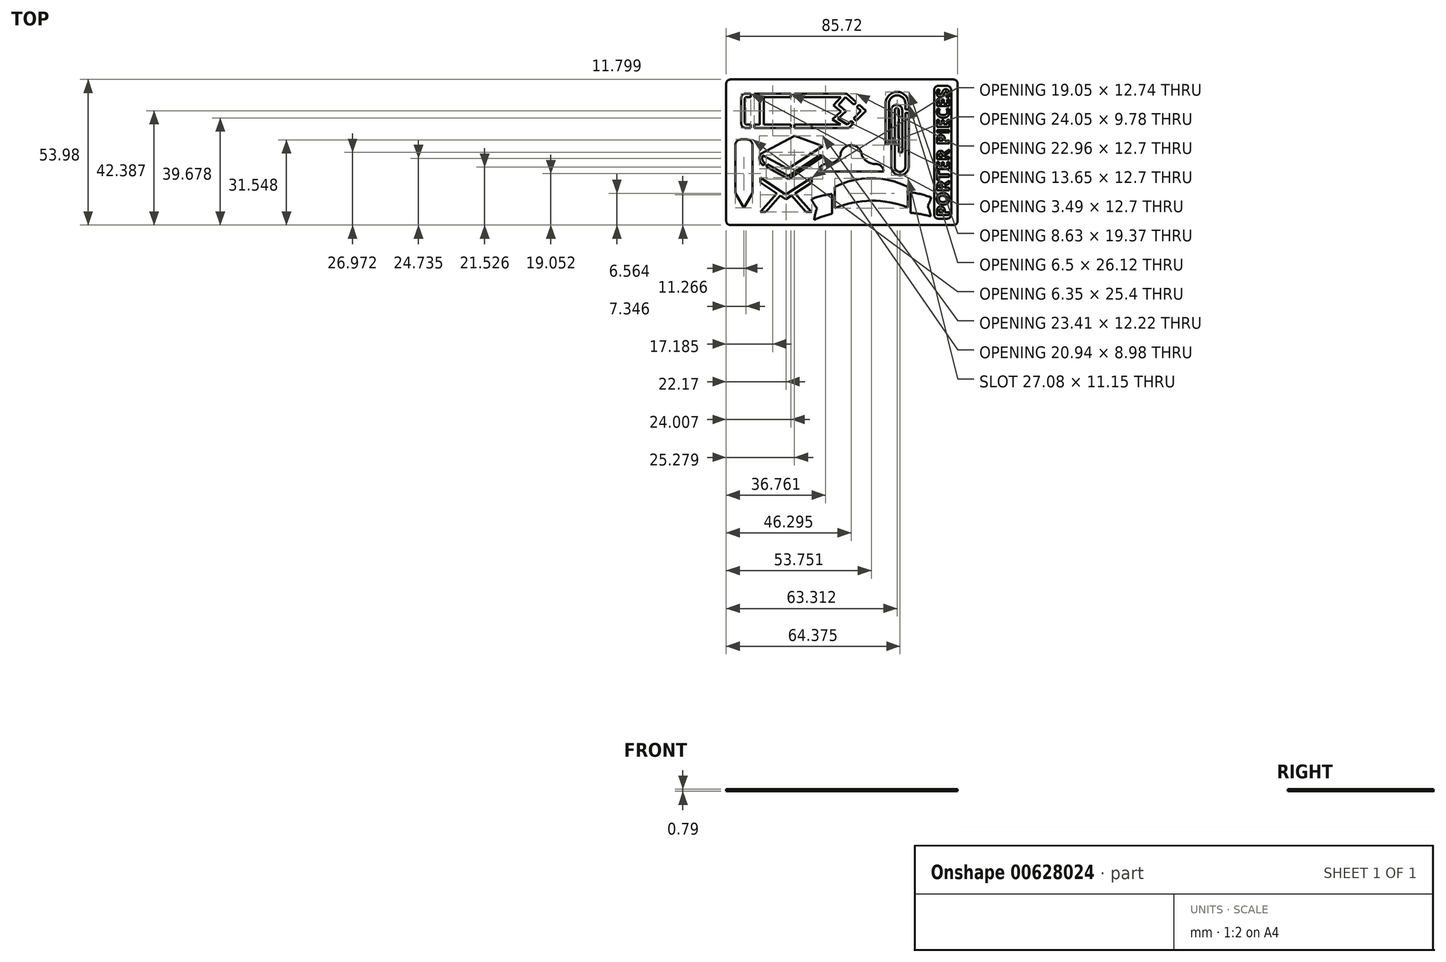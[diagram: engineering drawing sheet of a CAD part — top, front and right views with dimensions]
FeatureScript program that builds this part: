
annotation { "Feature Type Name" : "Feature", "Feature Type Description" : "" }
export const myFeature = defineFeature(function(context is Context, id is Id, definition is map)
    precondition{}
    {
        {
            var Q0;
            Q0=qCreatedBy(makeId("Top.planeOp"),FACE);
            var sketch = newSketch(context, id + "F0", { "sketchPlane" : qUnion([Q0])});
            skLineSegment(sketch, "E0.bottom", {"start": v(42.86, 26.99) * mm, "end": v(-42.86, 26.99) * mm});
            skLineSegment(sketch, "E0.top", {"start": v(42.86, -26.99) * mm, "end": v(-42.86, -26.99) * mm});
            skLineSegment(sketch, "E0.left", {"start": v(42.86, 26.99) * mm, "end": v(42.86, -26.99) * mm});
            skLineSegment(sketch, "E0.right", {"start": v(-42.86, 26.99) * mm, "end": v(-42.86, -26.99) * mm});
            skPoint(sketch, "E0.middle", {"position": v(0, 0) * mm});
            skSolve(sketch);
        }
        {
            var Q0;
            Q0=makeQuery(id+"F0.imprint","IMPRINT",FACE,{"disambiguationData":[TD([[makeQuery(id+"F0.imprint","IMPRINT",EDGE,{"derivedFrom":sQuery(id+"F0.wireOp",EDGE,"E0.bottom")}),1.0]])]});
            extrude(context, id + "F1", {"entities" : qUnion([Q0]), "depth" : 0.8 * mm, "offsetDistance" : 25.4 * mm});
        }
        {
            var Q0;
            Q0=makeQuery(id+"F1.opExtrude","SWEPT_EDGE",EDGE,{"disambiguationData":[OSD([sQuery(id+"F0.wireOp",EDGE,"E0.bottom"),sQuery(id+"F0.wireOp",EDGE,"E0.left")])]});
            var Q1;
            Q1=makeQuery(id+"F1.opExtrude","SWEPT_EDGE",EDGE,{"disambiguationData":[OSD([sQuery(id+"F0.wireOp",EDGE,"E0.bottom"),sQuery(id+"F0.wireOp",EDGE,"E0.right")])]});
            var Q2;
            Q2=makeQuery(id+"F1.opExtrude","SWEPT_EDGE",EDGE,{"disambiguationData":[OSD([sQuery(id+"F0.wireOp",EDGE,"E0.top"),sQuery(id+"F0.wireOp",EDGE,"E0.right")])]});
            var Q3;
            Q3=makeQuery(id+"F1.opExtrude","SWEPT_EDGE",EDGE,{"disambiguationData":[OSD([sQuery(id+"F0.wireOp",EDGE,"E0.top"),sQuery(id+"F0.wireOp",EDGE,"E0.left")])]});
            fillet(context, id + "F2", {"entities" : qUnion([Q0, Q1, Q2, Q3]), "radius" : 1.59 * mm, "tangentPropagation" : true, "allowEdgeOverflow" : false});
        }
        {
            var Q0;
            Q0=makeQuery(id+"F1.opExtrude","CAP_FACE",FACE,{"disambiguationData":[OSD([sQuery(id+"F0.wireOp",EDGE,"E0.bottom"),sQuery(id+"F0.wireOp",EDGE,"E0.top"),sQuery(id+"F0.wireOp",EDGE,"E0.left"),sQuery(id+"F0.wireOp",EDGE,"E0.right")])],"isStart":false});
            var sketch = newSketch(context, id + "F3", { "sketchPlane" : qUnion([Q0])});
            skLineSegment(sketch, "E1.bottom", {"start": v(34.13, -24.6) * mm, "end": v(40.48, -24.6) * mm});
            skLineSegment(sketch, "E1.top", {"start": v(34.13, 24.6) * mm, "end": v(40.48, 24.6) * mm});
            skLineSegment(sketch, "E1.left", {"start": v(34.13, -24.6) * mm, "end": v(34.13, 24.6) * mm});
            skLineSegment(sketch, "E1.right", {"start": v(40.48, -24.6) * mm, "end": v(40.48, 24.6) * mm});
            skSolve(sketch);
        }
        {
            var Q0;
            Q0=makeQuery(id+"F3.imprint","IMPRINT",FACE,{"disambiguationData":[TD([[makeQuery(id+"F3.imprint","IMPRINT",EDGE,{"derivedFrom":sQuery(id+"F3.wireOp",EDGE,"E1.bottom")}),1.0]])]});
            extrude(context, id + "F4", {"entities" : qUnion([Q0]), "operationType" : NewBodyOperationType.REMOVE, "oppositeDirection" : true, "depth" : 0.4 * mm, "offsetDistance" : 25.4 * mm});
        }
        {
            var Q0;
            Q0=makeQuery(id+"F4.boolean.opBoolean","COPY",EDGE,{"derivedFrom":makeQuery(id+"F4.opExtrude","SWEPT_EDGE",EDGE,{"disambiguationData":[OSD([sQuery(id+"F3.wireOp",EDGE,"E1.bottom"),sQuery(id+"F3.wireOp",EDGE,"E1.left")])]})});
            var Q1;
            Q1=makeQuery(id+"F4.boolean.opBoolean","COPY",EDGE,{"derivedFrom":makeQuery(id+"F4.opExtrude","SWEPT_EDGE",EDGE,{"disambiguationData":[OSD([sQuery(id+"F3.wireOp",EDGE,"E1.bottom"),sQuery(id+"F3.wireOp",EDGE,"E1.right")])]})});
            var Q2;
            Q2=makeQuery(id+"F4.boolean.opBoolean","COPY",EDGE,{"derivedFrom":makeQuery(id+"F4.opExtrude","SWEPT_EDGE",EDGE,{"disambiguationData":[OSD([sQuery(id+"F3.wireOp",EDGE,"E1.top"),sQuery(id+"F3.wireOp",EDGE,"E1.right")])]})});
            var Q3;
            Q3=makeQuery(id+"F4.boolean.opBoolean","COPY",EDGE,{"derivedFrom":makeQuery(id+"F4.opExtrude","SWEPT_EDGE",EDGE,{"disambiguationData":[OSD([sQuery(id+"F3.wireOp",EDGE,"E1.top"),sQuery(id+"F3.wireOp",EDGE,"E1.left")])]})});
            fillet(context, id + "F5", {"entities" : qUnion([Q0, Q1, Q2, Q3]), "radius" : 1.59 * mm, "tangentPropagation" : true, "allowEdgeOverflow" : false});
        }
        {
            var Q0;
            Q0=makeQuery(id+"F4.boolean.opBoolean","COPY",FACE,{"derivedFrom":makeQuery(id+"F4.opExtrude","CAP_FACE",FACE,{"disambiguationData":[OSD([sQuery(id+"F3.wireOp",EDGE,"E1.bottom"),sQuery(id+"F3.wireOp",EDGE,"E1.top"),sQuery(id+"F3.wireOp",EDGE,"E1.left"),sQuery(id+"F3.wireOp",EDGE,"E1.right")])],"isStart":false})});
            var sketch = newSketch(context, id + "F6", { "sketchPlane" : qUnion([Q0])});
            skText(sketch, "E2", { "text": "PORTER PIECES", "fontName": "OpenSans-Bold.ttf"});
            const initialGuessF6  = {"E2": [0.03976, -0.02381, 0, 1, 0.00461]};
            skSetInitialGuess(sketch, initialGuessF6);
            skSolve(sketch);
        }
        {
            var Q0;
            Q0=makeQuery(id+"F6.imprint","IMPRINT",FACE,{"disambiguationData":[TD([[makeQuery(id+"F6.imprint","IMPRINT",EDGE,{"derivedFrom":sQuery(id+"F6.wireOp",EDGE,"E2.sketch_text.stroke-0")}),-1.0]])]});
            var Q1;
            Q1=makeQuery(id+"F6.imprint","IMPRINT",FACE,{"disambiguationData":[TD([[makeQuery(id+"F6.imprint","IMPRINT",EDGE,{"derivedFrom":sQuery(id+"F6.wireOp",EDGE,"E2.sketch_text.stroke-16")}),-1.0]])]});
            var Q2;
            Q2=makeQuery(id+"F6.imprint","IMPRINT",FACE,{"disambiguationData":[TD([[makeQuery(id+"F6.imprint","IMPRINT",EDGE,{"derivedFrom":sQuery(id+"F6.wireOp",EDGE,"E2.sketch_text.stroke-30")}),-1.0]])]});
            var Q3;
            Q3=makeQuery(id+"F6.imprint","IMPRINT",FACE,{"disambiguationData":[TD([[makeQuery(id+"F6.imprint","IMPRINT",EDGE,{"derivedFrom":sQuery(id+"F6.wireOp",EDGE,"E2.sketch_text.stroke-49")}),-1.0]])]});
            var Q4;
            Q4=makeQuery(id+"F6.imprint","IMPRINT",FACE,{"disambiguationData":[TD([[makeQuery(id+"F6.imprint","IMPRINT",EDGE,{"derivedFrom":sQuery(id+"F6.wireOp",EDGE,"E2.sketch_text.stroke-57")}),-1.0]])]});
            var Q5;
            Q5=makeQuery(id+"F6.imprint","IMPRINT",FACE,{"disambiguationData":[TD([[makeQuery(id+"F6.imprint","IMPRINT",EDGE,{"derivedFrom":sQuery(id+"F6.wireOp",EDGE,"E2.sketch_text.stroke-69")}),-1.0]])]});
            var Q6;
            Q6=makeQuery(id+"F6.imprint","IMPRINT",FACE,{"disambiguationData":[TD([[makeQuery(id+"F6.imprint","IMPRINT",EDGE,{"derivedFrom":sQuery(id+"F6.wireOp",EDGE,"E2.sketch_text.stroke-88")}),-1.0]])]});
            var Q7;
            Q7=makeQuery(id+"F6.imprint","IMPRINT",FACE,{"disambiguationData":[TD([[makeQuery(id+"F6.imprint","IMPRINT",EDGE,{"derivedFrom":sQuery(id+"F6.wireOp",EDGE,"E2.sketch_text.stroke-104")}),-1.0]])]});
            var Q8;
            Q8=makeQuery(id+"F6.imprint","IMPRINT",FACE,{"disambiguationData":[TD([[makeQuery(id+"F6.imprint","IMPRINT",EDGE,{"derivedFrom":sQuery(id+"F6.wireOp",EDGE,"E2.sketch_text.stroke-108")}),-1.0]])]});
            var Q9;
            Q9=makeQuery(id+"F6.imprint","IMPRINT",FACE,{"disambiguationData":[TD([[makeQuery(id+"F6.imprint","IMPRINT",EDGE,{"derivedFrom":sQuery(id+"F6.wireOp",EDGE,"E2.sketch_text.stroke-120")}),-1.0]])]});
            var Q10;
            Q10=makeQuery(id+"F6.imprint","IMPRINT",FACE,{"disambiguationData":[TD([[makeQuery(id+"F6.imprint","IMPRINT",EDGE,{"derivedFrom":sQuery(id+"F6.wireOp",EDGE,"E2.sketch_text.stroke-135")}),-1.0]])]});
            var Q11;
            Q11=makeQuery(id+"F6.imprint","IMPRINT",FACE,{"disambiguationData":[TD([[makeQuery(id+"F6.imprint","IMPRINT",EDGE,{"derivedFrom":sQuery(id+"F6.wireOp",EDGE,"E2.sketch_text.stroke-147")}),-1.0]])]});
            extrude(context, id + "F7", {"entities" : qUnion([Q0, Q1, Q2, Q3, Q4, Q5, Q6, Q7, Q8, Q9, Q10, Q11]), "operationType" : NewBodyOperationType.ADD, "depth" : 0.4 * mm, "offsetDistance" : 25.4 * mm});
        }
        {
            var Q0;
            Q0=makeQuery(id+"F1.opExtrude","CAP_FACE",FACE,{"disambiguationData":[OSD([sQuery(id+"F0.wireOp",EDGE,"E0.bottom"),sQuery(id+"F0.wireOp",EDGE,"E0.top"),sQuery(id+"F0.wireOp",EDGE,"E0.left"),sQuery(id+"F0.wireOp",EDGE,"E0.right")])],"isStart":false});
            var sketch = newSketch(context, id + "F8", { "sketchPlane" : qUnion([Q0])});
            skLineSegment(sketch, "E3", {"start": v(-35.74, 21.75) * mm, "end": v(-33.77, 21.75) * mm});
            skLineSegment(sketch, "E4", {"start": v(1.84, 21.75) * mm, "end": v(5.38, 18.54) * mm});
            skLineSegment(sketch, "E5", {"start": v(8.86, 15.4) * mm, "end": v(5.22, 11.74) * mm});
            skLineSegment(sketch, "E6", {"start": v(2.55, 9.05) * mm, "end": v(-17.58, 9.05) * mm});
            skLineSegment(sketch, "E7", {"start": v(-37.26, 10.57) * mm, "end": v(-37.26, 20.22) * mm});
            skLineSegment(sketch, "E8", {"start": v(-37.26, 15.4) * mm, "end": v(17.01, 15.4) * mm, "construction": true});
            skPoint(sketch, "E9.visualSharp", {"position": v(-37.26, 21.75) * mm});
            skArc(sketch, "E9.filletArc", {"start": v(-35.74, 21.75) * mm, "mid": v(-36.81, 21.3) * mm, "end": v(-37.26, 20.22) * mm});
            skPoint(sketch, "E10.visualSharp", {"position": v(-37.26, 9.05) * mm});
            skArc(sketch, "E10.filletArc", {"start": v(-37.26, 10.57) * mm, "mid": v(-36.81, 9.5) * mm, "end": v(-35.74, 9.05) * mm});
            skLineSegment(sketch, "E11.left", {"start": v(-30.5, 20.48) * mm, "end": v(-30.5, 10.32) * mm});
            skLineSegment(sketch, "E11.right", {"start": v(-28.99, 20.48) * mm, "end": v(-28.99, 10.32) * mm});
            skLineSegment(sketch, "E12.0", {"start": v(1.35, 20.48) * mm, "end": v(4.53, 17.6) * mm});
            skLineSegment(sketch, "E12.1", {"start": v(-35.23, 20.48) * mm, "end": v(-33.77, 20.48) * mm});
            skLineSegment(sketch, "E12.2", {"start": v(7.02, 15.35) * mm, "end": v(4.32, 12.63) * mm});
            skLineSegment(sketch, "E12.3", {"start": v(-0.42, 10.32) * mm, "end": v(-17.58, 10.32) * mm});
            skLineSegment(sketch, "E12.4", {"start": v(-36, 11.08) * mm, "end": v(-36, 19.71) * mm});
            skLineSegment(sketch, "E13", {"start": v(1.35, 20.48) * mm, "end": v(-1.3, 17.55) * mm});
            skLineSegment(sketch, "E14", {"start": v(-1.3, 17.55) * mm, "end": v(1.57, 15.23) * mm});
            skLineSegment(sketch, "E15", {"start": v(1.57, 15.23) * mm, "end": v(-1.44, 12.42) * mm});
            skLineSegment(sketch, "E16", {"start": v(-1.44, 12.42) * mm, "end": v(2.02, 10.32) * mm});
            skLineSegment(sketch, "E17.0", {"start": v(-3.53, 12.2) * mm, "end": v(-0.42, 10.32) * mm});
            skLineSegment(sketch, "E17.1", {"start": v(-0.36, 15.16) * mm, "end": v(-3.53, 12.2) * mm});
            skLineSegment(sketch, "E17.2", {"start": v(-3.14, 17.4) * mm, "end": v(-0.36, 15.16) * mm});
            skLineSegment(sketch, "E17.3", {"start": v(-0.37, 20.48) * mm, "end": v(-3.14, 17.4) * mm});
            skLineSegment(sketch, "E18.trimOffspring", {"start": v(-28.99, 20.48) * mm, "end": v(-18.85, 20.48) * mm});
            skLineSegment(sketch, "E19.trimOffspring", {"start": v(-30.5, 10.32) * mm, "end": v(-32.5, 10.32) * mm});
            skPoint(sketch, "E20.visualSharp", {"position": v(-36, 20.48) * mm});
            skArc(sketch, "E20.filletArc", {"start": v(-35.23, 20.48) * mm, "mid": v(-35.77, 20.25) * mm, "end": v(-36, 19.71) * mm});
            skPoint(sketch, "E21.visualSharp", {"position": v(-36, 10.32) * mm});
            skArc(sketch, "E21.filletArc", {"start": v(-36, 11.08) * mm, "mid": v(-35.77, 10.54) * mm, "end": v(-35.23, 10.32) * mm});
            skLineSegment(sketch, "E22.left", {"start": v(-18.85, 21.75) * mm, "end": v(-18.85, 20.48) * mm});
            skLineSegment(sketch, "E22.right", {"start": v(-17.58, 21.75) * mm, "end": v(-17.58, 20.48) * mm});
            skLineSegment(sketch, "E23.trimOffspring", {"start": v(-18.85, 10.32) * mm, "end": v(-18.85, 9.05) * mm});
            skLineSegment(sketch, "E24.trimOffspring", {"start": v(-17.58, 10.32) * mm, "end": v(-17.58, 9.05) * mm});
            skLineSegment(sketch, "E25.trimOffspring", {"start": v(-17.58, 21.75) * mm, "end": v(1.84, 21.75) * mm});
            skLineSegment(sketch, "E26.trimOffspring", {"start": v(-17.58, 20.48) * mm, "end": v(-0.37, 20.48) * mm});
            skLineSegment(sketch, "E27.trimOffspring", {"start": v(-18.85, 10.32) * mm, "end": v(-28.99, 10.32) * mm});
            skLineSegment(sketch, "E28.trimOffspring", {"start": v(-18.85, 9.05) * mm, "end": v(-32.5, 9.05) * mm});
            skLineSegment(sketch, "E29.left", {"start": v(-33.77, 21.75) * mm, "end": v(-33.77, 20.48) * mm});
            skLineSegment(sketch, "E29.right", {"start": v(-32.5, 21.75) * mm, "end": v(-32.5, 20.48) * mm});
            skLineSegment(sketch, "E30.trimOffspring", {"start": v(-32.5, 21.75) * mm, "end": v(-18.85, 21.75) * mm});
            skLineSegment(sketch, "E31.trimOffspring", {"start": v(-32.5, 20.48) * mm, "end": v(-30.5, 20.48) * mm});
            skLineSegment(sketch, "E32.trimOffspring", {"start": v(-32.5, 10.32) * mm, "end": v(-32.5, 9.05) * mm});
            skLineSegment(sketch, "E33.trimOffspring", {"start": v(-33.77, 10.32) * mm, "end": v(-33.77, 9.05) * mm});
            skLineSegment(sketch, "E34.trimOffspring", {"start": v(-33.77, 10.32) * mm, "end": v(-35.23, 10.32) * mm});
            skLineSegment(sketch, "E35.trimOffspring", {"start": v(-33.77, 9.05) * mm, "end": v(-35.74, 9.05) * mm});
            skLineSegment(sketch, "E36.left", {"start": v(5.38, 18.54) * mm, "end": v(4.53, 17.6) * mm});
            skLineSegment(sketch, "E36.right", {"start": v(6.33, 17.69) * mm, "end": v(5.47, 16.74) * mm});
            skLineSegment(sketch, "E37.trimOffspring", {"start": v(5.47, 16.74) * mm, "end": v(7.02, 15.35) * mm});
            skLineSegment(sketch, "E38.trimOffspring", {"start": v(6.33, 17.69) * mm, "end": v(8.86, 15.4) * mm});
            skLineSegment(sketch, "E39.left", {"start": v(3.42, 11.73) * mm, "end": v(4.32, 10.83) * mm});
            skLineSegment(sketch, "E39.right", {"start": v(4.32, 12.63) * mm, "end": v(5.22, 11.74) * mm});
            skLineSegment(sketch, "E40.trimOffspring", {"start": v(3.42, 11.73) * mm, "end": v(2.02, 10.32) * mm});
            skLineSegment(sketch, "E41.trimOffspring", {"start": v(4.32, 10.83) * mm, "end": v(2.55, 9.05) * mm});
            skSolve(sketch);
        }
        {
            var Q0;
            Q0 = qSketchRegion(id + "F8", true);
            extrude(context, id + "F9", {"entities" : qUnion([Q0]), "operationType" : NewBodyOperationType.REMOVE, "oppositeDirection" : true, "depth" : 25.4 * mm, "offsetDistance" : 25.4 * mm});
        }
        {
            var Q0;
            Q0=makeQuery(id+"F1.opExtrude","CAP_FACE",FACE,{"disambiguationData":[OSD([sQuery(id+"F0.wireOp",EDGE,"E0.bottom"),sQuery(id+"F0.wireOp",EDGE,"E0.top"),sQuery(id+"F0.wireOp",EDGE,"E0.left"),sQuery(id+"F0.wireOp",EDGE,"E0.right")])],"isStart":false});
            var sketch = newSketch(context, id + "F10", { "sketchPlane" : qUnion([Q0])});
            skLineSegment(sketch, "E42", {"start": v(17.4, 3) * mm, "end": v(17.4, 18.06) * mm});
            skArc(sketch, "E43", {"start": v(23.5, 18.06) * mm, "mid": v(20.45, 21.1) * mm, "end": v(17.4, 18.06) * mm});
            skLineSegment(sketch, "E44", {"start": v(23.5, 18.06) * mm, "end": v(23.5, 15.88) * mm});
            skArc(sketch, "E45", {"start": v(19.53, -5.25) * mm, "mid": v(21.51, -7.23) * mm, "end": v(23.5, -5.25) * mm});
            skLineSegment(sketch, "E46", {"start": v(19.53, -5.25) * mm, "end": v(19.53, 15.59) * mm});
            skArc(sketch, "E47", {"start": v(21.06, 15.59) * mm, "mid": v(20.3, 16.35) * mm, "end": v(19.53, 15.59) * mm});
            skLineSegment(sketch, "E48", {"start": v(21.06, 15.59) * mm, "end": v(21.06, 0) * mm});
            skLineSegment(sketch, "E49.0", {"start": v(22.33, 15.59) * mm, "end": v(22.33, 0) * mm});
            skArc(sketch, "E49.1", {"start": v(22.33, 15.59) * mm, "mid": v(20.3, 17.62) * mm, "end": v(18.26, 15.59) * mm});
            skLineSegment(sketch, "E49.2", {"start": v(18.26, -5.25) * mm, "end": v(18.26, 15.59) * mm});
            skLineSegment(sketch, "E49.3", {"start": v(16.14, 3) * mm, "end": v(16.14, 18.06) * mm});
            skArc(sketch, "E49.4", {"start": v(24.77, 18.06) * mm, "mid": v(20.45, 22.37) * mm, "end": v(16.14, 18.06) * mm});
            skLineSegment(sketch, "E49.5", {"start": v(24.77, 18.06) * mm, "end": v(24.77, 15.88) * mm});
            skArc(sketch, "E49.6", {"start": v(18.26, -5.25) * mm, "mid": v(21.51, -8.5) * mm, "end": v(24.77, -5.25) * mm});
            skLineSegment(sketch, "E50", {"start": v(16.14, 3) * mm, "end": v(17.4, 3) * mm});
            skLineSegment(sketch, "E51", {"start": v(21.06, 0) * mm, "end": v(22.33, 0) * mm});
            skLineSegment(sketch, "E52.bottom", {"start": v(23.5, 15.88) * mm, "end": v(24.77, 15.88) * mm});
            skLineSegment(sketch, "E52.top", {"start": v(23.5, 14.6) * mm, "end": v(24.77, 14.6) * mm});
            skLineSegment(sketch, "E53.trimOffspring", {"start": v(23.5, 14.6) * mm, "end": v(23.5, -5.25) * mm});
            skLineSegment(sketch, "E54.trimOffspring", {"start": v(24.77, 14.6) * mm, "end": v(24.77, -5.25) * mm});
            skSolve(sketch);
        }
        {
            var Q0;
            Q0 = qSketchRegion(id + "F10", true);
            extrude(context, id + "F11", {"entities" : qUnion([Q0]), "operationType" : NewBodyOperationType.REMOVE, "oppositeDirection" : true, "depth" : 25.4 * mm, "offsetDistance" : 25.4 * mm});
        }
        {
            var Q0;
            Q0=makeQuery(id+"F1.opExtrude","CAP_FACE",FACE,{"disambiguationData":[OSD([sQuery(id+"F0.wireOp",EDGE,"E0.bottom"),sQuery(id+"F0.wireOp",EDGE,"E0.top"),sQuery(id+"F0.wireOp",EDGE,"E0.left"),sQuery(id+"F0.wireOp",EDGE,"E0.right")])],"isStart":false});
            var sketch = newSketch(context, id + "F12", { "sketchPlane" : qUnion([Q0])});
            skLineSegment(sketch, "E55", {"start": v(-37.44, 4.76) * mm, "end": v(-35.15, 4.76) * mm});
            skLineSegment(sketch, "E56", {"start": v(-33.12, 2.73) * mm, "end": v(-33.12, -15.14) * mm});
            skLineSegment(sketch, "E57", {"start": v(-33.12, -15.14) * mm, "end": v(-36.3, -20.64) * mm});
            skLineSegment(sketch, "E58", {"start": v(-36.3, -20.64) * mm, "end": v(-39.47, -15.14) * mm});
            skLineSegment(sketch, "E59", {"start": v(-39.47, -15.14) * mm, "end": v(-39.47, 2.73) * mm});
            skPoint(sketch, "E60.visualSharp", {"position": v(-39.47, 4.76) * mm});
            skArc(sketch, "E60.filletArc", {"start": v(-37.44, 4.76) * mm, "mid": v(-38.88, 4.17) * mm, "end": v(-39.47, 2.73) * mm});
            skPoint(sketch, "E61.visualSharp", {"position": v(-33.12, 4.76) * mm});
            skArc(sketch, "E61.filletArc", {"start": v(-33.12, 2.73) * mm, "mid": v(-33.72, 4.17) * mm, "end": v(-35.15, 4.76) * mm});
            skSolve(sketch);
        }
        {
            var Q0;
            Q0=makeQuery(id+"F12.imprint","IMPRINT",FACE,{"disambiguationData":[TD([[makeQuery(id+"F12.imprint","IMPRINT",EDGE,{"derivedFrom":sQuery(id+"F12.wireOp",EDGE,"E55")}),-1.0]])]});
            extrude(context, id + "F13", {"entities" : qUnion([Q0]), "operationType" : NewBodyOperationType.REMOVE, "oppositeDirection" : true, "depth" : 25.4 * mm, "offsetDistance" : 25.4 * mm});
        }
        {
            var Q0;
            Q0=makeQuery(id+"F1.opExtrude","CAP_FACE",FACE,{"disambiguationData":[OSD([sQuery(id+"F0.wireOp",EDGE,"E0.bottom"),sQuery(id+"F0.wireOp",EDGE,"E0.top"),sQuery(id+"F0.wireOp",EDGE,"E0.left"),sQuery(id+"F0.wireOp",EDGE,"E0.right")])],"isStart":false});
            var sketch = newSketch(context, id + "F14", { "sketchPlane" : qUnion([Q0])});
            skLineSegment(sketch, "E62", {"start": v(-30.2, -0.66) * mm, "end": v(-17.5, 6.1) * mm});
            skLineSegment(sketch, "E63", {"start": v(-17.5, 6.1) * mm, "end": v(-7.15, 2.33) * mm});
            skLineSegment(sketch, "E64", {"start": v(-7.15, 2.33) * mm, "end": v(-20.1, -6.13) * mm});
            skLineSegment(sketch, "E65", {"start": v(-20.1, -6.13) * mm, "end": v(-29.28, -1.15) * mm});
            skLineSegment(sketch, "E66", {"start": v(-29.65, -4.45) * mm, "end": v(-28.94, -4.85) * mm});
            skLineSegment(sketch, "E67", {"start": v(-19.77, -9.96) * mm, "end": v(-7.11, -1.53) * mm});
            skArc(sketch, "E68", {"start": v(-30.2, -0.66) * mm, "mid": v(-30.42, -1.24) * mm, "end": v(-30.54, -1.86) * mm});
            skLineSegment(sketch, "E69.0", {"start": v(-19.81, -8.74) * mm, "end": v(-8.15, -0.97) * mm});
            skLineSegment(sketch, "E69.1", {"start": v(-28.99, -3.63) * mm, "end": v(-28.42, -3.94) * mm});
            skArc(sketch, "E69.2", {"start": v(-29.26, -1.12) * mm, "mid": v(-29.44, -1.61) * mm, "end": v(-29.5, -2.13) * mm});
            skLineSegment(sketch, "E70", {"start": v(-7.11, -1.53) * mm, "end": v(-8.15, -0.97) * mm});
            skArc(sketch, "E71.trimOffspring", {"start": v(-30.51, -2.65) * mm, "mid": v(-30.22, -3.62) * mm, "end": v(-29.65, -4.45) * mm});
            skArc(sketch, "E72.trimOffspring", {"start": v(-29.36, -2.96) * mm, "mid": v(-29.2, -3.31) * mm, "end": v(-28.99, -3.63) * mm});
            skArc(sketch, "E73", {"start": v(-30.54, -1.86) * mm, "mid": v(-30.56, -2.26) * mm, "end": v(-30.51, -2.65) * mm});
            skArc(sketch, "E74", {"start": v(-29.5, -2.13) * mm, "mid": v(-29.51, -2.56) * mm, "end": v(-29.36, -2.96) * mm});
            skLineSegment(sketch, "E75.left", {"start": v(-28.42, -3.94) * mm, "end": v(-28.94, -4.85) * mm});
            skLineSegment(sketch, "E75.right", {"start": v(-27.53, -4.44) * mm, "end": v(-28.05, -5.34) * mm});
            skLineSegment(sketch, "E76.trimOffspring", {"start": v(-27.53, -4.44) * mm, "end": v(-19.81, -8.74) * mm});
            skLineSegment(sketch, "E77.trimOffspring", {"start": v(-28.05, -5.34) * mm, "end": v(-19.77, -9.96) * mm});
            skSolve(sketch);
        }
        {
            var Q0;
            Q0 = qSketchRegion(id + "F14", true);
            extrude(context, id + "F15", {"entities" : qUnion([Q0]), "operationType" : NewBodyOperationType.REMOVE, "oppositeDirection" : true, "depth" : 25.4 * mm, "offsetDistance" : 25.4 * mm});
        }
        {
            var Q0;
            Q0=makeQuery(id+"F1.opExtrude","CAP_FACE",FACE,{"disambiguationData":[OSD([sQuery(id+"F0.wireOp",EDGE,"E0.bottom"),sQuery(id+"F0.wireOp",EDGE,"E0.top"),sQuery(id+"F0.wireOp",EDGE,"E0.left"),sQuery(id+"F0.wireOp",EDGE,"E0.right")])],"isStart":false});
            var sketch = newSketch(context, id + "F16", { "sketchPlane" : qUnion([Q0])});
            skArc(sketch, "E78", {"start": v(3.43, 2.64) * mm, "mid": v(0.7, 1.54) * mm, "end": v(-0.52, -1.15) * mm});
            skArc(sketch, "E79", {"start": v(-5.53, -4.33) * mm, "mid": v(-7.67, -5.08) * mm, "end": v(-8.6, -7.15) * mm});
            skArc(sketch, "E80", {"start": v(-5.77, -4.32) * mm, "mid": v(-2.66, -3.53) * mm, "end": v(-0.52, -1.15) * mm});
            skLineSegment(sketch, "E81", {"start": v(-8.6, -7.15) * mm, "end": v(3.43, -7.15) * mm});
            skArc(sketch, "E82.MirrorCS", {"start": v(12.4, -4.33) * mm, "mid": v(14.54, -5.08) * mm, "end": v(15.46, -7.15) * mm});
            skArc(sketch, "E83.MirrorCS", {"start": v(12.64, -4.32) * mm, "mid": v(9.53, -3.53) * mm, "end": v(7.4, -1.15) * mm});
            skArc(sketch, "E84.MirrorCS", {"start": v(3.43, 2.64) * mm, "mid": v(6.17, 1.54) * mm, "end": v(7.4, -1.15) * mm});
            skLineSegment(sketch, "E85", {"start": v(3.43, -7.15) * mm, "end": v(15.46, -7.15) * mm});
            skSolve(sketch);
        }
        {
            var Q0;
            Q0 = qSketchRegion(id + "F16", true);
            extrude(context, id + "F17", {"entities" : qUnion([Q0]), "operationType" : NewBodyOperationType.REMOVE, "oppositeDirection" : true, "depth" : 25.4 * mm, "offsetDistance" : 25.4 * mm});
        }
        {
            var Q0;
            Q0=makeQuery(id+"F1.opExtrude","CAP_FACE",FACE,{"disambiguationData":[OSD([sQuery(id+"F0.wireOp",EDGE,"E0.bottom"),sQuery(id+"F0.wireOp",EDGE,"E0.top"),sQuery(id+"F0.wireOp",EDGE,"E0.left"),sQuery(id+"F0.wireOp",EDGE,"E0.right")])],"isStart":false});
            var sketch = newSketch(context, id + "F18", { "sketchPlane" : qUnion([Q0])});
            skLineSegment(sketch, "E86", {"start": v(-30.21, -9.36) * mm, "end": v(-20.74, -15.58) * mm});
            skLineSegment(sketch, "E87", {"start": v(-20.74, -15.58) * mm, "end": v(-11.16, -9.36) * mm});
            skLineSegment(sketch, "E88.0", {"start": v(-20.74, -17.4) * mm, "end": v(-18.68, -16.06) * mm});
            skLineSegment(sketch, "E88.1", {"start": v(-30.21, -11.18) * mm, "end": v(-24.1, -15.2) * mm});
            skLineSegment(sketch, "E89", {"start": v(-30.21, -22.06) * mm, "end": v(-24.1, -15.2) * mm});
            skLineSegment(sketch, "E90", {"start": v(-28.16, -22.06) * mm, "end": v(-22.8, -16.05) * mm});
            skLineSegment(sketch, "E91.MirrorCS", {"start": v(-13.35, -22.1) * mm, "end": v(-18.68, -16.06) * mm});
            skLineSegment(sketch, "E92.MirrorCS", {"start": v(-11.3, -22.1) * mm, "end": v(-17.39, -15.22) * mm});
            skLineSegment(sketch, "E93.trimOffspring", {"start": v(-11.34, -22.06) * mm, "end": v(-11.16, -22.06) * mm});
            skLineSegment(sketch, "E94.trimOffspring", {"start": v(-17.39, -15.22) * mm, "end": v(-11.16, -11.17) * mm});
            skLineSegment(sketch, "E95.trimOffspring", {"start": v(-22.8, -16.05) * mm, "end": v(-20.74, -17.4) * mm});
            skLineSegment(sketch, "E96", {"start": v(-30.21, -9.36) * mm, "end": v(-30.21, -11.18) * mm});
            skLineSegment(sketch, "E97", {"start": v(-30.21, -22.06) * mm, "end": v(-28.16, -22.06) * mm});
            skLineSegment(sketch, "E98", {"start": v(-13.35, -22.1) * mm, "end": v(-11.16, -22.06) * mm});
            skLineSegment(sketch, "E99", {"start": v(-11.16, -9.36) * mm, "end": v(-11.16, -11.17) * mm});
            skSolve(sketch);
        }
        {
            var Q0;
            Q0 = qSketchRegion(id + "F18", true);
            extrude(context, id + "F19", {"entities" : qUnion([Q0]), "operationType" : NewBodyOperationType.REMOVE, "oppositeDirection" : true, "depth" : 25.4 * mm, "offsetDistance" : 25.4 * mm});
        }
        {
            var Q0;
            Q0=makeQuery(id+"F1.opExtrude","CAP_FACE",FACE,{"disambiguationData":[OSD([sQuery(id+"F0.wireOp",EDGE,"E0.bottom"),sQuery(id+"F0.wireOp",EDGE,"E0.top"),sQuery(id+"F0.wireOp",EDGE,"E0.left"),sQuery(id+"F0.wireOp",EDGE,"E0.right")])],"isStart":false});
            var sketch = newSketch(context, id + "F20", { "sketchPlane" : qUnion([Q0])});
            skLineSegment(sketch, "E100", {"start": v(-2.65, -20.77) * mm, "end": v(-2.65, -12.8) * mm});
            skArc(sketch, "E101", {"start": v(24.43, -12.8) * mm, "mid": v(10.9, -9.61) * mm, "end": v(-2.65, -12.8) * mm});
            skLineSegment(sketch, "E102", {"start": v(24.43, -12.8) * mm, "end": v(24.43, -20.5) * mm});
            skArc(sketch, "E103", {"start": v(24.43, -20.5) * mm, "mid": v(10.86, -17.94) * mm, "end": v(-2.65, -20.77) * mm});
            skSolve(sketch);
        }
        {
            var Q0;
            Q0=makeQuery(id+"F20.imprint","IMPRINT",FACE,{"disambiguationData":[TD([[makeQuery(id+"F20.imprint","IMPRINT",EDGE,{"derivedFrom":sQuery(id+"F20.wireOp",EDGE,"E100")}),-1.0]])]});
            extrude(context, id + "F21", {"entities" : qUnion([Q0]), "operationType" : NewBodyOperationType.REMOVE, "oppositeDirection" : true, "depth" : 25.4 * mm, "offsetDistance" : 25.4 * mm});
        }
        {
            var Q0;
            Q0=makeQuery(id+"F1.opExtrude","CAP_FACE",FACE,{"disambiguationData":[OSD([sQuery(id+"F0.wireOp",EDGE,"E0.bottom"),sQuery(id+"F0.wireOp",EDGE,"E0.top"),sQuery(id+"F0.wireOp",EDGE,"E0.left"),sQuery(id+"F0.wireOp",EDGE,"E0.right")])],"isStart":false});
            var sketch = newSketch(context, id + "F22", { "sketchPlane" : qUnion([Q0])});
            skArc(sketch, "E104", {"start": v(-3.67, -15.5) * mm, "mid": v(-7.53, -16.16) * mm, "end": v(-11.29, -17.32) * mm});
            skArc(sketch, "E105", {"start": v(-3.67, -22.73) * mm, "mid": v(-7.03, -23.74) * mm, "end": v(-10.29, -25.07) * mm});
            skLineSegment(sketch, "E106", {"start": v(-3.67, -15.5) * mm, "end": v(-3.67, -22.73) * mm});
            skArc(sketch, "E107", {"start": v(-9.24, -20.64) * mm, "mid": v(-9.88, -22.83) * mm, "end": v(-10.29, -25.07) * mm});
            skArc(sketch, "E108", {"start": v(-11.29, -17.32) * mm, "mid": v(-10.42, -19.08) * mm, "end": v(-9.24, -20.64) * mm});
            skSolve(sketch);
        }
        {
            var Q0;
            Q0 = qSketchRegion(id + "F22", true);
            extrude(context, id + "F23", {"entities" : qUnion([Q0]), "operationType" : NewBodyOperationType.REMOVE, "oppositeDirection" : true, "depth" : 25.4 * mm, "offsetDistance" : 25.4 * mm});
        }
        {
            var Q0;
            Q0=makeQuery(id+"F1.opExtrude","CAP_FACE",FACE,{"disambiguationData":[OSD([sQuery(id+"F0.wireOp",EDGE,"E0.bottom"),sQuery(id+"F0.wireOp",EDGE,"E0.top"),sQuery(id+"F0.wireOp",EDGE,"E0.left"),sQuery(id+"F0.wireOp",EDGE,"E0.right")])],"isStart":false});
            var sketch = newSketch(context, id + "F24", { "sketchPlane" : qUnion([Q0])});
            skLineSegment(sketch, "E109", {"start": v(25.45, -14.83) * mm, "end": v(25.45, -22.42) * mm});
            skArc(sketch, "E110.MirrorCS", {"start": v(25.45, -22.42) * mm, "mid": v(29.2, -22.91) * mm, "end": v(32.9, -23.78) * mm});
            skArc(sketch, "E111.MirrorCS", {"start": v(33.07, -16.73) * mm, "mid": v(32.54, -18.32) * mm, "end": v(31.78, -19.81) * mm});
            skArc(sketch, "E112.MirrorCS", {"start": v(25.45, -14.83) * mm, "mid": v(29.32, -15.54) * mm, "end": v(33.07, -16.73) * mm});
            skArc(sketch, "E113.MirrorCS", {"start": v(31.78, -19.81) * mm, "mid": v(32.43, -21.77) * mm, "end": v(32.9, -23.78) * mm});
            skSolve(sketch);
        }
        {
            var Q0;
            Q0 = qSketchRegion(id + "F24", true);
            extrude(context, id + "F25", {"entities" : qUnion([Q0]), "operationType" : NewBodyOperationType.REMOVE, "oppositeDirection" : true, "depth" : 25.4 * mm, "offsetDistance" : 25.4 * mm});
        }
    });
